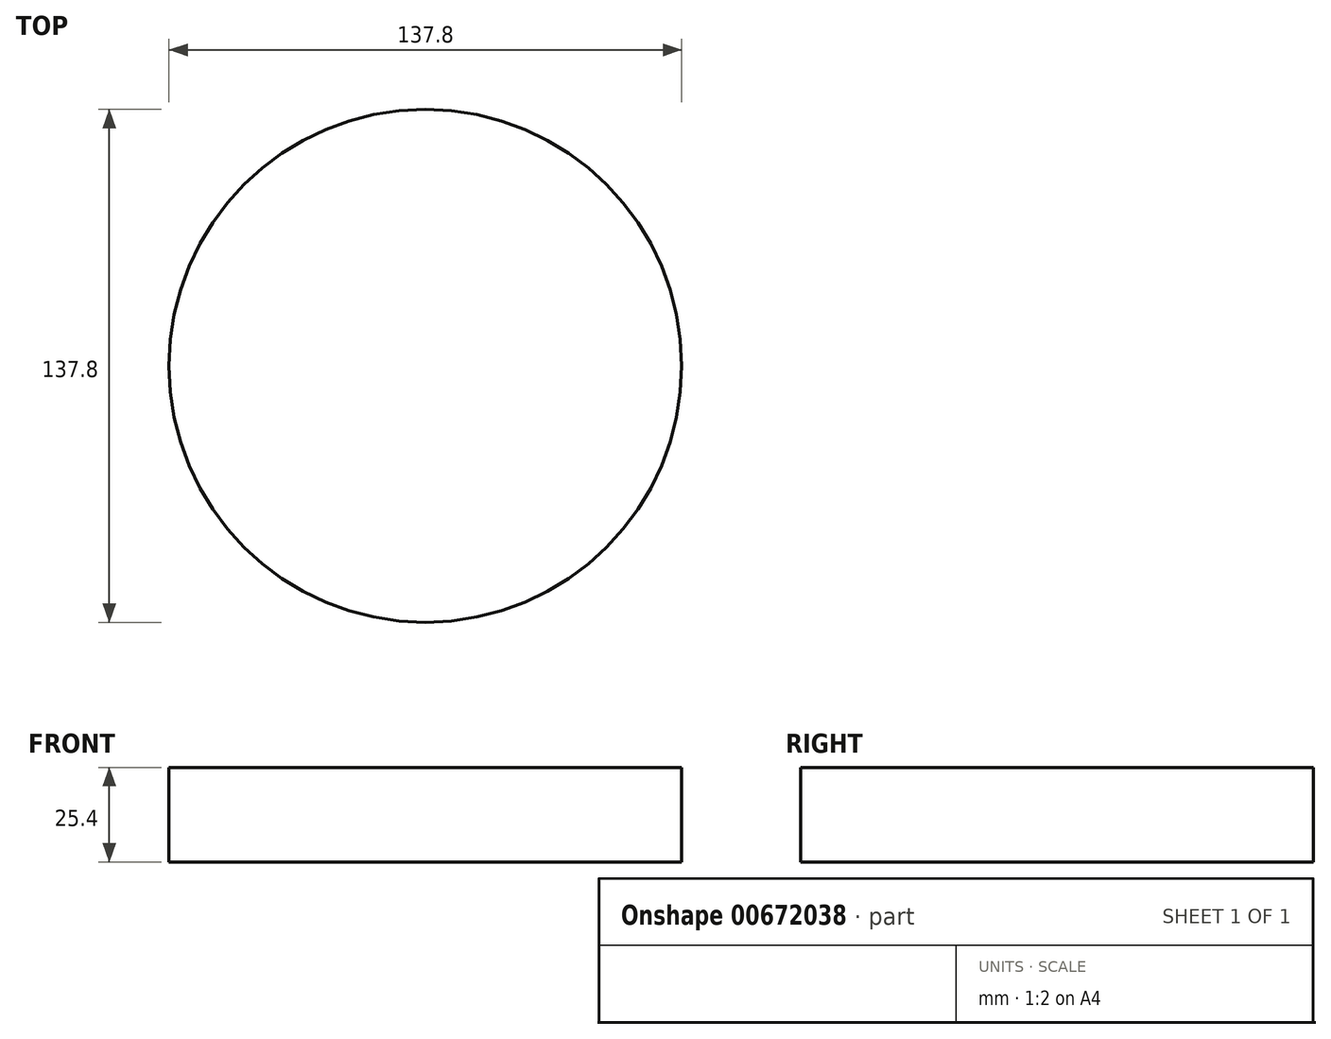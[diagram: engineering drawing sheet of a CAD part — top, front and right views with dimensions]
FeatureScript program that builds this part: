
annotation { "Feature Type Name" : "Feature", "Feature Type Description" : "" }
export const myFeature = defineFeature(function(context is Context, id is Id, definition is map)
    precondition{}
    {
        {
            var Q0;
            Q0=qCreatedBy(makeId("Top.planeOp"),FACE);
            var sketch = newSketch(context, id + "F0", { "sketchPlane" : qUnion([Q0])});
            skCircle(sketch, "E0", {"center": v(0, 0) * mm, "radius": 68.9 * mm});
            skSolve(sketch);
        }
        {
            var Q0;
            Q0 = qSketchRegion(id + "F0", true);
            extrude(context, id + "F1", {"entities" : qUnion([Q0]), "depth" : 25.4 * mm, "offsetDistance" : 25.4 * mm});
        }
    });
